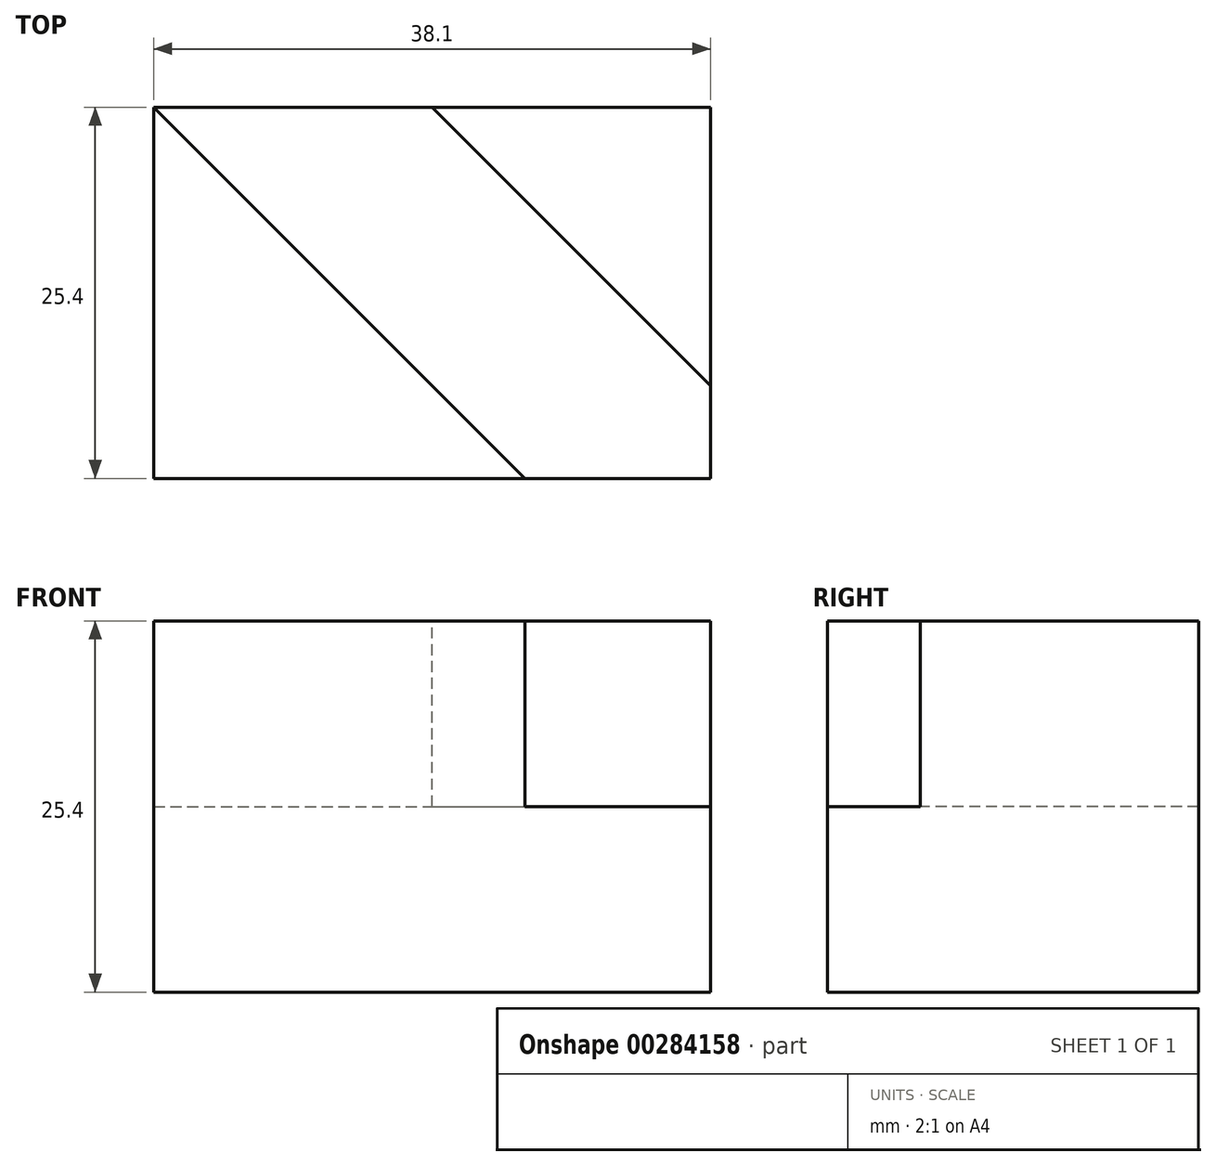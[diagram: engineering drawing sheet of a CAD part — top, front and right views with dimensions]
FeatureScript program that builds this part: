
annotation { "Feature Type Name" : "Feature", "Feature Type Description" : "" }
export const myFeature = defineFeature(function(context is Context, id is Id, definition is map)
    precondition{}
    {
        {
            var Q0;
            Q0=qCreatedBy(makeId("Top.planeOp"),FACE);
            var sketch = newSketch(context, id + "F0", { "sketchPlane" : qUnion([Q0])});
            skLineSegment(sketch, "E0", {"start": v(0, 0) * mm, "end": v(0, 25.4) * mm});
            skLineSegment(sketch, "E1", {"start": v(0, 25.4) * mm, "end": v(38.1, 25.4) * mm});
            skLineSegment(sketch, "E2", {"start": v(38.1, 25.4) * mm, "end": v(38.1, 0) * mm});
            skLineSegment(sketch, "E3", {"start": v(38.1, 0) * mm, "end": v(0, 0) * mm});
            skLineSegment(sketch, "E4", {"start": v(0, 25.4) * mm, "end": v(25.4, 0) * mm});
            skLineSegment(sketch, "E5", {"start": v(19.05, 25.4) * mm, "end": v(38.1, 6.35) * mm});
            skSolve(sketch);
        }
        {
            var Q0;
            {var subQ0=sQuery(id+"F0.wireOp",EDGE,"E0");Q0=makeQuery(id+"F0.imprint","IMPRINT",FACE,{"disambiguationData":[TD([[makeQuery(id+"F0.imprint","IMPRINT",EDGE,{"derivedFrom":subQ0}),-1.0]])]});}
            var Q1;
            {var subQ3=sQuery(id+"F0.wireOp",EDGE,"E5");Q1=makeQuery(id+"F0.imprint","IMPRINT",FACE,{"disambiguationData":[TD([[makeQuery(id+"F0.imprint","IMPRINT",EDGE,{"derivedFrom":subQ3}),1.0]])]});}
            var Q2;
            {var subQ0=sQuery(id+"F0.wireOp",EDGE,"E4");Q2=makeQuery(id+"F0.imprint","IMPRINT",FACE,{"disambiguationData":[TD([[makeQuery(id+"F0.imprint","IMPRINT",EDGE,{"derivedFrom":subQ0}),1.0]])]});}
            extrude(context, id + "F1", {"entities" : qUnion([Q0, Q1, Q2]), "oppositeDirection" : true, "depth" : 25.4 * mm});
        }
        {
            var Q0;
            {var subQ0=sQuery(id+"F0.wireOp",EDGE,"E4");Q0=makeQuery(id+"F0.imprint","IMPRINT",FACE,{"disambiguationData":[TD([[makeQuery(id+"F0.imprint","IMPRINT",EDGE,{"derivedFrom":subQ0}),1.0]])]});}
            extrude(context, id + "F2", {"entities" : qUnion([Q0]), "operationType" : NewBodyOperationType.REMOVE, "oppositeDirection" : true, "depth" : 12.7 * mm});
        }
    });
